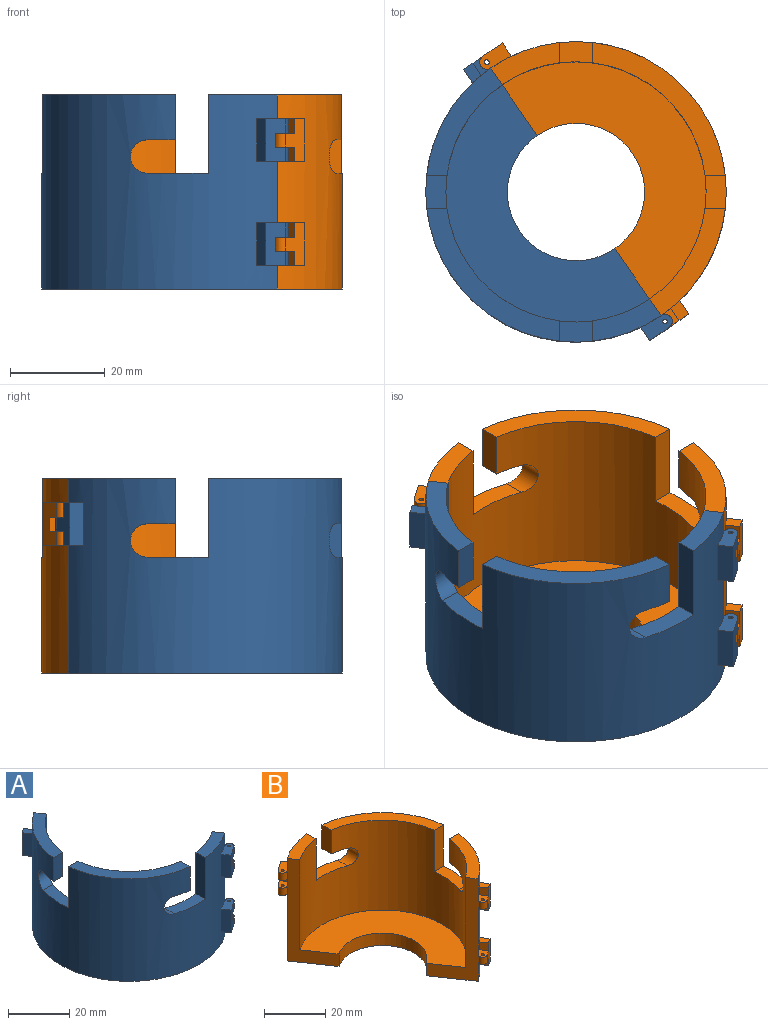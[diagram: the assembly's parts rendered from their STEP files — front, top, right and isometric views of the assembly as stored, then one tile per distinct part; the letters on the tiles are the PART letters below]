
ASSEMBLY  parts=2 mates=1
PART A: 54 faces, bbox 52.1x60.6x41 mm
  f0: cylinder r=31.75mm len=57.91mm, axis (0,0,-1), area 3610.7mm2, adj f1,f3,f6,f8,f11,f12,f14,f15
  f1: plane 6.69x5.57mm, normal (0,0,1), area 18.4mm2, adj f0,f38,f39,f41,f43
  f2: plane 4.47x4.15mm, normal (0,0,-1), area 10.3mm2, adj f5,f37,f39,f41,f43
  f3: plane 6.69x5.57mm, normal (0,0,-1), area 18.4mm2, adj f0,f38,f39,f40,f42
  f4: plane 4.47x4.15mm, normal (0,0,1), area 10.3mm2, adj f5,f37,f39,f40,f42
  f5: cylinder r=31.75mm len=2.87mm, axis (0,0,-1), area 7.2mm2, adj f2,f4,f28,f37
  f6: plane 6.69x5.57mm, normal (0,0,1), area 18.4mm2, adj f0,f31,f32,f34,f36
  f7: plane 4.47x4.15mm, normal (0,0,-1), area 10.3mm2, adj f10,f30,f32,f34,f36
  f8: plane 6.69x5.57mm, normal (0,0,-1), area 18.4mm2, adj f0,f31,f32,f33,f35
  f9: plane 4.47x4.15mm, normal (0,0,1), area 10.3mm2, adj f10,f30,f32,f33,f35
  f10: cylinder r=31.75mm len=2.87mm, axis (0,0,-1), area 7.2mm2, adj f7,f9,f28,f30
  f11: plane 22.66x15.97mm, normal (0,0,1), area 107mm2, adj f0,f13,f27,f29
  f12: plane 28.06x28.06mm, normal (0,0,1), area 168mm2, adj f0,f13,f21,f26
  f13: cylinder r=27.5mm len=50.16mm, axis (0,0,-1), area 2749.9mm2, adj f11,f12,f14,f17,f18,f19,f20,f21
  f14: plane 14.49x8.9mm, normal (0,0,1), area 60.9mm2, adj f0,f13,f22,f28
  f15: plane 57.91x49.74mm, normal (0,0,-1), area 1253.2mm2, adj f0,f16,f28,f29
  f16: cylinder r=14.5mm len=26.45mm, axis (0,0,-1), area 227.8mm2, adj f15,f17,f28,f29
  f17: plane 50.16x43.08mm, normal (0,0,1), area 857.7mm2, adj f13,f16,f28,f29
  f18: plane 6x5.75mm, normal (0,0,-1), area 26.2mm2, adj f0,f13,f19,f21
  f19: cylinder r=3.5mm len=7mm, axis (0,-1,0), area 51mm2, adj f0,f13,f18,f20
  f20: plane 13x5.94mm, normal (0,0,1), area 56mm2, adj f0,f13,f19,f22
  f21: plane 9.5x4.28mm, normal (1,0,0), area 40.7mm2, adj f0,f12,f13,f18
  f22: plane 16.5x4.28mm, normal (-1,0,0), area 70.6mm2, adj f0,f13,f14,f20
  f23: plane 6x5.75mm, normal (0,0,-1), area 26.2mm2, adj f0,f13,f24,f27
  f24: cylinder r=3.5mm len=7mm, axis (-1,0,0), area 51mm2, adj f0,f13,f23,f25
  f25: plane 13x5.94mm, normal (0,0,1), area 56mm2, adj f0,f13,f24,f26
  f26: plane 16.5x4.28mm, normal (0,1,0), area 70.6mm2, adj f0,f12,f13,f25
  f27: plane 9.5x4.28mm, normal (0,-1,0), area 40.7mm2, adj f0,f11,f13,f23
  f28: plane 41x14.21mm, normal (0.82,0.57,0), area 239.3mm2, adj f0,f5,f10,f13,f14,f15,f16,f17
  f29: plane 41x14.21mm, normal (0.82,0.57,0), area 239.3mm2, adj f0,f11,f13,f15,f16,f17,f53
  f30: plane 2.87x2.55mm, normal (0.82,0.57,0), area 8.9mm2, adj f7,f9,f10,f32
  f31: plane 9x2.8mm, normal (-0.82,-0.57,0), area 30.6mm2, adj f0,f6,f8,f32
  f32: plane 9x4.12mm, normal (0.57,-0.82,0), area 37.8mm2, adj f6,f7,f8,f9,f30,f31,f35,f36
  f33: cylinder r=0.5mm len=3mm, axis (0,0,1), area 9.4mm2, adj f8,f9
  f34: cylinder r=0.5mm len=3.13mm, axis (0,0,1), area 9.8mm2, adj f6,f7
  f35: cylinder r=1.5mm len=3mm, axis (0,0,1), area 14.1mm2, adj f8,f9,f28,f32
  f36: cylinder r=1.5mm len=3.13mm, axis (0,0,1), area 14.8mm2, adj f6,f7,f28,f32
  f37: plane 2.87x2.55mm, normal (0.82,0.57,0), area 8.9mm2, adj f2,f4,f5,f39
  f38: plane 9x2.8mm, normal (-0.82,-0.57,0), area 30.6mm2, adj f0,f1,f3,f39
  f39: plane 9x4.12mm, normal (0.57,-0.82,0), area 37.8mm2, adj f1,f2,f3,f4,f37,f38,f42,f43
  f40: cylinder r=0.5mm len=3mm, axis (0,0,1), area 9.4mm2, adj f3,f4
  f41: cylinder r=0.5mm len=3.13mm, axis (0,0,1), area 9.8mm2, adj f1,f2
  f42: cylinder r=1.5mm len=3mm, axis (0,0,1), area 14.1mm2, adj f3,f4,f28,f39
  f43: cylinder r=1.5mm len=3.13mm, axis (0,0,1), area 14.8mm2, adj f1,f2,f28,f39
  f44: cylinder r=0.5mm len=2.87mm, axis (0,0,1), area 9mm2, adj f50,f51
  f45: plane 3x2.55mm, normal (0.82,0.57,0), area 9.3mm2, adj f0,f46,f51,f52
  f46: plane 4.22x3.82mm, normal (0,0,-1), area 8.1mm2, adj f0,f45,f47,f52
  f47: plane 9x2.8mm, normal (-0.82,-0.57,0), area 30.6mm2, adj f0,f46,f48,f52
  f48: plane 4.22x3.82mm, normal (0,0,1), area 8.1mm2, adj f0,f47,f49,f52
  f49: plane 3.13x2.55mm, normal (0.82,0.57,0), area 9.7mm2, adj f0,f48,f50,f52
  f50: plane 4.41x4.23mm, normal (0,0,1), area 10.3mm2, adj f0,f44,f49,f52,f53
  f51: plane 4.41x4.23mm, normal (0,0,-1), area 10.3mm2, adj f0,f44,f45,f52,f53
  f52: plane 9x4.12mm, normal (-0.57,0.82,0), area 29.7mm2, adj f45,f46,f47,f48,f49,f50,f51,f53
  f53: cylinder r=1.5mm len=2.87mm, axis (0,0,1), area 13.5mm2, adj f29,f50,f51,f52
PART B: 52 faces, bbox 52.1x60.6x41 mm
  f0: cylinder r=31.75mm len=2.87mm, axis (0,0,-1), area 7.2mm2, adj f3,f41,f46,f47
  f1: plane 9x4.12mm, normal (0.57,-0.82,0), area 29.7mm2, adj f32,f33,f34,f35,f36,f37,f38,f40
  f2: plane 9x4.12mm, normal (0.57,-0.82,0), area 29.7mm2, adj f23,f24,f25,f26,f27,f28,f29,f31
  f3: plane 41x14.21mm, normal (-0.82,-0.57,0), area 239.3mm2, adj f0,f16,f17,f18,f19,f20,f21,f50
  f4: plane 16.5x4.28mm, normal (1,0,0), area 70.6mm2, adj f5,f19,f20,f21
  f5: plane 13x5.94mm, normal (0,0,1), area 56mm2, adj f4,f6,f19,f21
  f6: cylinder r=3.5mm len=7mm, axis (0,1,0), area 51mm2, adj f5,f7,f19,f21
  f7: plane 6x5.75mm, normal (0,0,-1), area 26.2mm2, adj f6,f8,f19,f21
  f8: plane 9.5x4.28mm, normal (-1,0,0), area 40.7mm2, adj f7,f9,f19,f21
  f9: plane 28.06x28.06mm, normal (0,0,1), area 168mm2, adj f8,f10,f19,f21
  f10: plane 16.5x4.28mm, normal (0,-1,0), area 70.6mm2, adj f9,f11,f19,f21
  f11: plane 13x5.94mm, normal (0,0,1), area 56mm2, adj f10,f12,f19,f21
  f12: cylinder r=3.5mm len=7mm, axis (1,0,0), area 51mm2, adj f11,f13,f19,f21
  f13: plane 6x5.75mm, normal (0,0,-1), area 26.2mm2, adj f12,f14,f19,f21
  f14: plane 9.5x4.28mm, normal (0,1,0), area 40.7mm2, adj f13,f15,f19,f21
  f15: plane 22.66x15.97mm, normal (0,0,1), area 107mm2, adj f14,f19,f21,f22
  f16: plane 50.16x43.08mm, normal (0,0,1), area 857.7mm2, adj f3,f17,f19,f22
  f17: cylinder r=14.5mm len=26.45mm, axis (0,0,-1), area 227.8mm2, adj f3,f16,f18,f22
  f18: plane 57.91x49.74mm, normal (0,0,-1), area 1253.2mm2, adj f3,f17,f21,f22
  f19: cylinder r=27.5mm len=50.16mm, axis (0,0,-1), area 2749.9mm2, adj f3,f4,f5,f6,f7,f8,f9,f10
  f20: plane 14.49x8.9mm, normal (0,0,1), area 60.9mm2, adj f3,f4,f19,f21
  f21: cylinder r=31.75mm len=57.91mm, axis (0,0,-1), area 3626.1mm2, adj f3,f4,f5,f6,f7,f8,f9,f10
  f22: plane 41x14.21mm, normal (-0.82,-0.57,0), area 239.3mm2, adj f15,f16,f17,f18,f19,f21,f31,f40
  f23: plane 3.13x2.55mm, normal (-0.82,-0.57,0), area 9.7mm2, adj f2,f21,f27,f28
  f24: plane 9x2.8mm, normal (0.82,0.57,0), area 30.6mm2, adj f2,f21,f28,f29
  f25: plane 3x2.55mm, normal (-0.82,-0.57,0), area 9.3mm2, adj f2,f21,f26,f29
  f26: plane 4.41x4.23mm, normal (0,0,-1), area 10.3mm2, adj f2,f21,f25,f30,f31
  f27: plane 4.41x4.23mm, normal (0,0,1), area 10.3mm2, adj f2,f21,f23,f30,f31
  f28: plane 4.22x3.82mm, normal (0,0,1), area 8.1mm2, adj f2,f21,f23,f24
  f29: plane 4.22x3.82mm, normal (0,0,-1), area 8.1mm2, adj f2,f21,f24,f25
  f30: cylinder r=0.5mm len=2.87mm, axis (0,0,1), area 9mm2, adj f26,f27
  f31: cylinder r=1.5mm len=2.87mm, axis (0,0,1), area 13.5mm2, adj f2,f22,f26,f27
  f32: plane 3.13x2.55mm, normal (-0.82,-0.57,0), area 9.7mm2, adj f1,f21,f36,f37
  f33: plane 9x2.8mm, normal (0.82,0.57,0), area 30.6mm2, adj f1,f21,f37,f38
  f34: plane 3x2.55mm, normal (-0.82,-0.57,0), area 9.3mm2, adj f1,f21,f35,f38
  f35: plane 4.41x4.23mm, normal (0,0,-1), area 10.3mm2, adj f1,f21,f34,f39,f40
  f36: plane 4.41x4.23mm, normal (0,0,1), area 10.3mm2, adj f1,f21,f32,f39,f40
  f37: plane 4.22x3.82mm, normal (0,0,1), area 8.1mm2, adj f1,f21,f32,f33
  f38: plane 4.22x3.82mm, normal (0,0,-1), area 8.1mm2, adj f1,f21,f33,f34
  f39: cylinder r=0.5mm len=2.87mm, axis (0,0,1), area 9mm2, adj f35,f36
  f40: cylinder r=1.5mm len=2.87mm, axis (0,0,1), area 13.5mm2, adj f1,f22,f35,f36
  f41: plane 2.87x2.55mm, normal (-0.82,-0.57,0), area 8.9mm2, adj f0,f46,f47,f49
  f42: cylinder r=0.5mm len=3mm, axis (0,0,1), area 9.4mm2, adj f45,f46
  f43: plane 9x2.8mm, normal (0.82,0.57,0), area 30.6mm2, adj f21,f45,f48,f49
  f44: cylinder r=0.5mm len=3.13mm, axis (0,0,1), area 9.8mm2, adj f47,f48
  f45: plane 6.69x5.57mm, normal (0,0,-1), area 18.4mm2, adj f21,f42,f43,f49,f51
  f46: plane 4.47x4.15mm, normal (0,0,1), area 10.3mm2, adj f0,f41,f42,f49,f51
  f47: plane 4.47x4.15mm, normal (0,0,-1), area 10.3mm2, adj f0,f41,f44,f49,f50
  f48: plane 6.69x5.57mm, normal (0,0,1), area 18.4mm2, adj f21,f43,f44,f49,f50
  f49: plane 9x4.12mm, normal (-0.57,0.82,0), area 37.8mm2, adj f41,f43,f45,f46,f47,f48,f50,f51
  f50: cylinder r=1.5mm len=3.13mm, axis (0,0,1), area 14.8mm2, adj f3,f47,f48,f49
  f51: cylinder r=1.5mm len=3mm, axis (0,0,1), area 14.1mm2, adj f3,f45,f46,f49
PLACE A at identity fixed
PLACE B rot(axis=(0,0,-1),0deg) t=(0,0,0)mm
MATE revolute B.f31 <-> A.f33  axis (0,0,1) through (18.84,-27.4,32.87)mm
